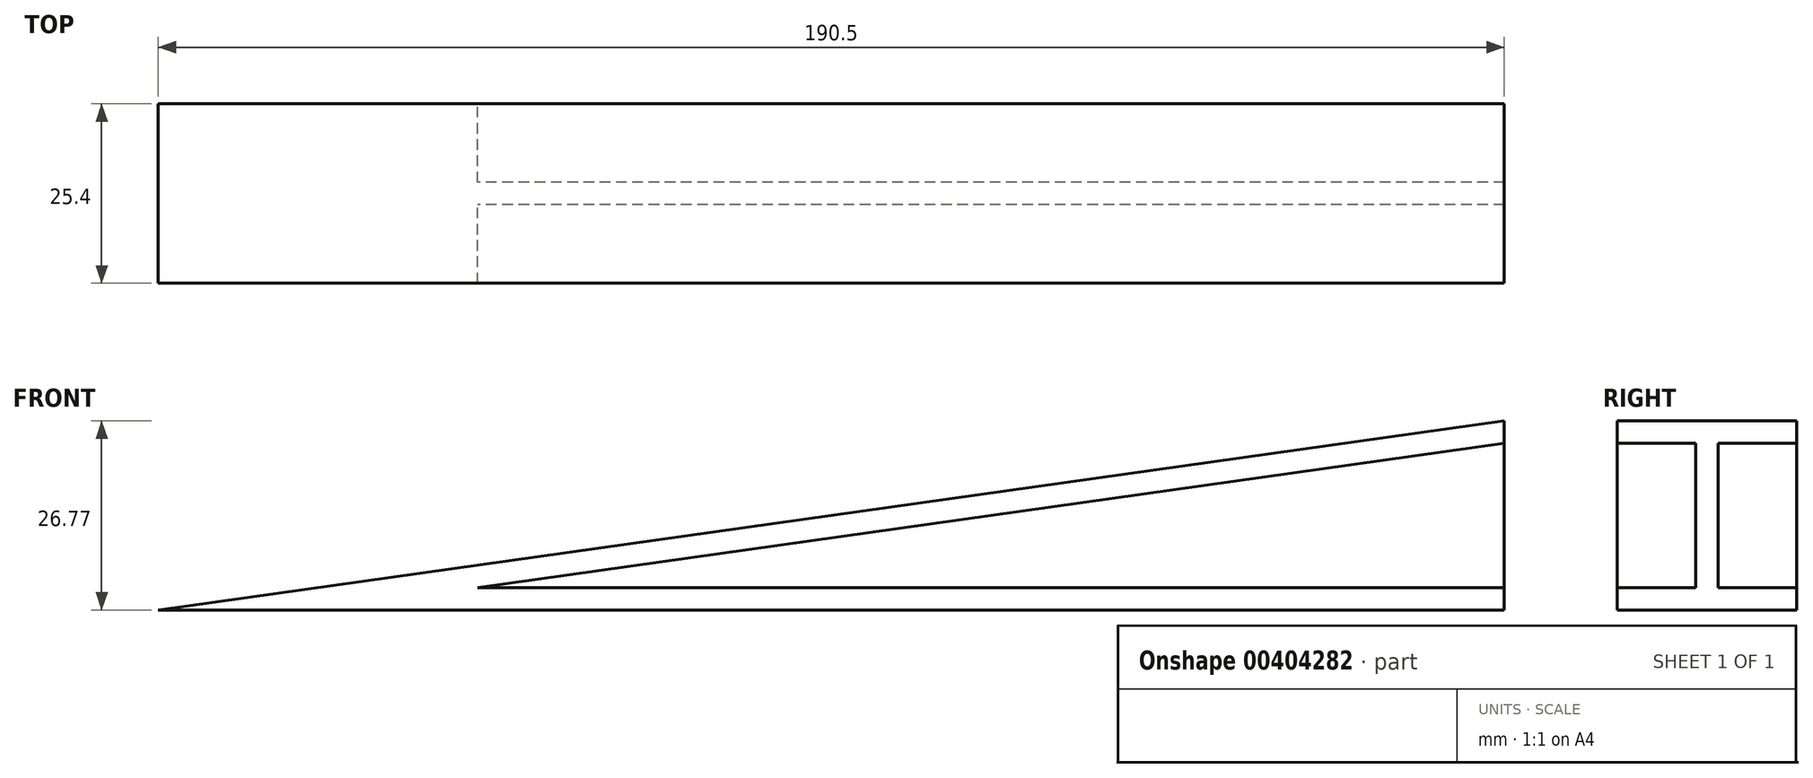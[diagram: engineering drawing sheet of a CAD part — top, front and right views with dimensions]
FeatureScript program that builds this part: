
annotation { "Feature Type Name" : "Feature", "Feature Type Description" : "" }
export const myFeature = defineFeature(function(context is Context, id is Id, definition is map)
    precondition{}
    {
        {
            var Q0;
            Q0=qCreatedBy(makeId("Front.planeOp"),FACE);
            var sketch = newSketch(context, id + "F0", { "sketchPlane" : qUnion([Q0])});
            skLineSegment(sketch, "E0", {"start": v(-103.52, 0) * mm, "end": v(86.98, 0) * mm});
            skLineSegment(sketch, "E1", {"start": v(-103.52, 0) * mm, "end": v(86.98, 26.77) * mm});
            skLineSegment(sketch, "E2", {"start": v(86.98, 0) * mm, "end": v(86.98, 26.77) * mm});
            skPoint(sketch, "E3", {"position": v(86.98, 23.6) * mm});
            skPoint(sketch, "E4", {"position": v(86.98, 3.17) * mm});
            skLineSegment(sketch, "E5", {"start": v(86.98, 23.6) * mm, "end": v(-61.81, 2.69) * mm});
            skLineSegment(sketch, "E6", {"start": v(86.98, 3.17) * mm, "end": v(-61.81, 3.17) * mm});
            skSolve(sketch);
        }
        {
            var Q0;
            {var subQ0=sQuery(id+"F0.wireOp",EDGE,"E5");var subQ1=sQuery(id+"F0.wireOp",EDGE,"E2");var subQ2=makeQuery(id+"F0.imprint","INTERSECT",VERTEX,{"derivedFrom":[subQ1,subQ0]});Q0=makeQuery(id+"F0.imprint","IMPRINT",FACE,{"disambiguationData":[TD([[makeQuery(id+"F0.imprint","IMPRINT",EDGE,{"disambiguationData":[TD([[subQ2,1.0]])],"derivedFrom":subQ1}),1.0]])]});}
            extrude(context, id + "F1", {"entities" : qUnion([Q0]), "endBound" : BoundingType.SYMMETRIC, "depth" : 3.17 * mm});
        }
        {
            var Q0;
            {var subQ4=sQuery(id+"F0.wireOp",EDGE,"E0");Q0=makeQuery(id+"F0.imprint","IMPRINT",FACE,{"disambiguationData":[TD([[makeQuery(id+"F0.imprint","IMPRINT",EDGE,{"derivedFrom":subQ4}),1.0]])]});}
            extrude(context, id + "F2", {"entities" : qUnion([Q0]), "operationType" : NewBodyOperationType.ADD, "endBound" : BoundingType.SYMMETRIC, "depth" : 25.4 * mm});
        }
    });
